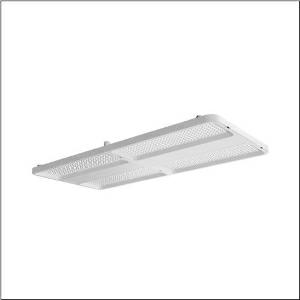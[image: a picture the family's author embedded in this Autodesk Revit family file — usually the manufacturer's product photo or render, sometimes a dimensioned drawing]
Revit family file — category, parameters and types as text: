
# Revit family: highbay_11_maxi_51hn12db4mda
name_source: partatom
category: Lighting Fixtures
units: mm (PartAtom-declared; Revit-internal decimal feet)

## family parameters
Cut with Voids When Loaded = No
Host = Face
Light Source = No
Part Type = Normal
Room Calculation Point = No
Round Connector Dimension = Use Diameter
Shared = No

## types (1)
- --- (1 x LED, 4620 lm, 22.4 W, 4000K)
    Apparent Load = 22 VA
    CIE Flux Codes = 87 98 100 100 100
    Color Rendering = 80
    Color Temperature = 4000K
    Default Elevation = 1800 mm
    Description = high bay luminaire Highbay 11 maxi; direct symmetric wide distribution, light control with lens of PMMA; UGR ≤ 22 (X = 4H | Y = 8H | S = 0.25H | reflection values 70/50/20); luminous flux: 30.000lm; light colour: 840, colour temperature: 4000K, MacAdam ≤ 2 SDCM (initial), colour rendering: CRI > 80; luminous efficacy: 204,8lm/W; rated service life: 100.000h (L95) at AT= 25°C; control: DALI 2; luminaire connection: terminal, 5-pole, max. 2.5mm² (cable entry for one cable, Ø 8.5..16mm); mains connection: 230..240V, AC/DC 0/50..60Hz; connected load: 146,5W; protection rating (complete): IP66; insulation class (complete): insulation class I (protective earthing); protection symbol: D; impact resistance: IK08; certification: CE, ENEC, VDE, UKCA; luminaire for central battery installations according to EN 60598-2-22, internal wiring halogen-free; luminaire LABS conformity tested according to VDMA 24364:2018-05; Suitable for use in the food industry according to the specifications of IFS-Food, HACCP and/or BRC; housing frame of high-performance plastic PA6, matt traffic white (RAL 9016); cover of PMMA; dimension (LxWxH): 946 x 442 x 72mm; permissible operating ambient temperature: -40..+60°C (reducing of maximum allowable ambient temperature of 5°C with ceiling mounting); packaging unit: 1 piece; (delivery without accessories; please order mounting accessories separately)
    Height = 72 mm  [stored 0.23622 ft]
    Lamp = 1 x LED
    Lamp Light Flux = 4620 lm
    Lamp Power = 22.4 W
    Lamp count = 1
    Length = 946 mm
    Luminous efficacy = 206 lm/W
    Manufacturer = Siteco
    ModVariant = No
    Model = 51HN12DB4MDA
    Mounting Place = Ceiling
    Mounting Type = Pendant
    Number of Poles = 1
    OnlyDefault = Yes
    Power Factor = 1
    Product Name = Highbay 11 maxi
    Product group = high bay luminaire
    ProductGroupID = 902
    Protection Class = Protection class I
    Protection Degree = IP 66
    RLX_Detail_Level = 1
    RLX_Emergency_Light_Flux = 0 lm
    RLX_Emergency_Type = 0
    RLX_Emergency_Type_DB = No
    RlxData = <blob elided: 127305 chars, md5=17856828>
    Socket = socket
    Standby Power = 0 W
    System Light Flux = 4620 lm
    System Power = 22 W
    Type Comments = : DC mode (central or group accumulator) initial emergency light level
    Type Image = l_1363244.jpg
    URL = http://relux.com
    VarID = @adj_024907
    Voltage = 0 V
    Weight = 0.00 kg
    Width = 442 mm

note: [stored X ft] marks values corroborated as IEEE doubles in the binary element streams (Revit-internal decimal feet)

## geometry (parser evidence)
native form markers: Blend x4, Sweep x12
no freeform markers — native parametric forms only
